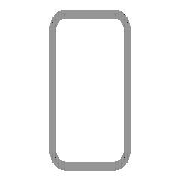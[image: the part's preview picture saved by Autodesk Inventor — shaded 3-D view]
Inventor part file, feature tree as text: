
AUTODESK INVENTOR PART (.ipt)
format: ipt  version: 2017 (Build 210142000, 142)  size: 127,488 bytes
history: native  units: mm (DEFAULTED — no unit token found)
features: other x4, sketch x3, plane x1
ambient origin geometry x8: Origin, YZ Plane, XZ Plane, XY Plane, X Axis, Y Axis, Z Axis, Center Point
bodies: Solid1 (feature_tree), Body (feature_tree)
feature tree (8):
  parser-record x1  (decoder bookkeeping rows leaked as tree rows — omitted from the tree; the rows remain in map.json)
  other  "Driven Length"
  other  "Start plane"
  other  "End plane"
  sketch  "Sketch"  dims[d10=203.2mm d11=76.2mm d12=6.35mm d13=-0.0mm d14=2438.4mm d15=101.6mm d16=38.1mm d17=12.7mm d18=90.0deg d19=2438.4mm]
  sketch  "Sketch3"  dims[d3=2438.4mm]
  plane  "Work Plane3"
  sketch  "Sketch4"  dims[d4=0.0mm]
